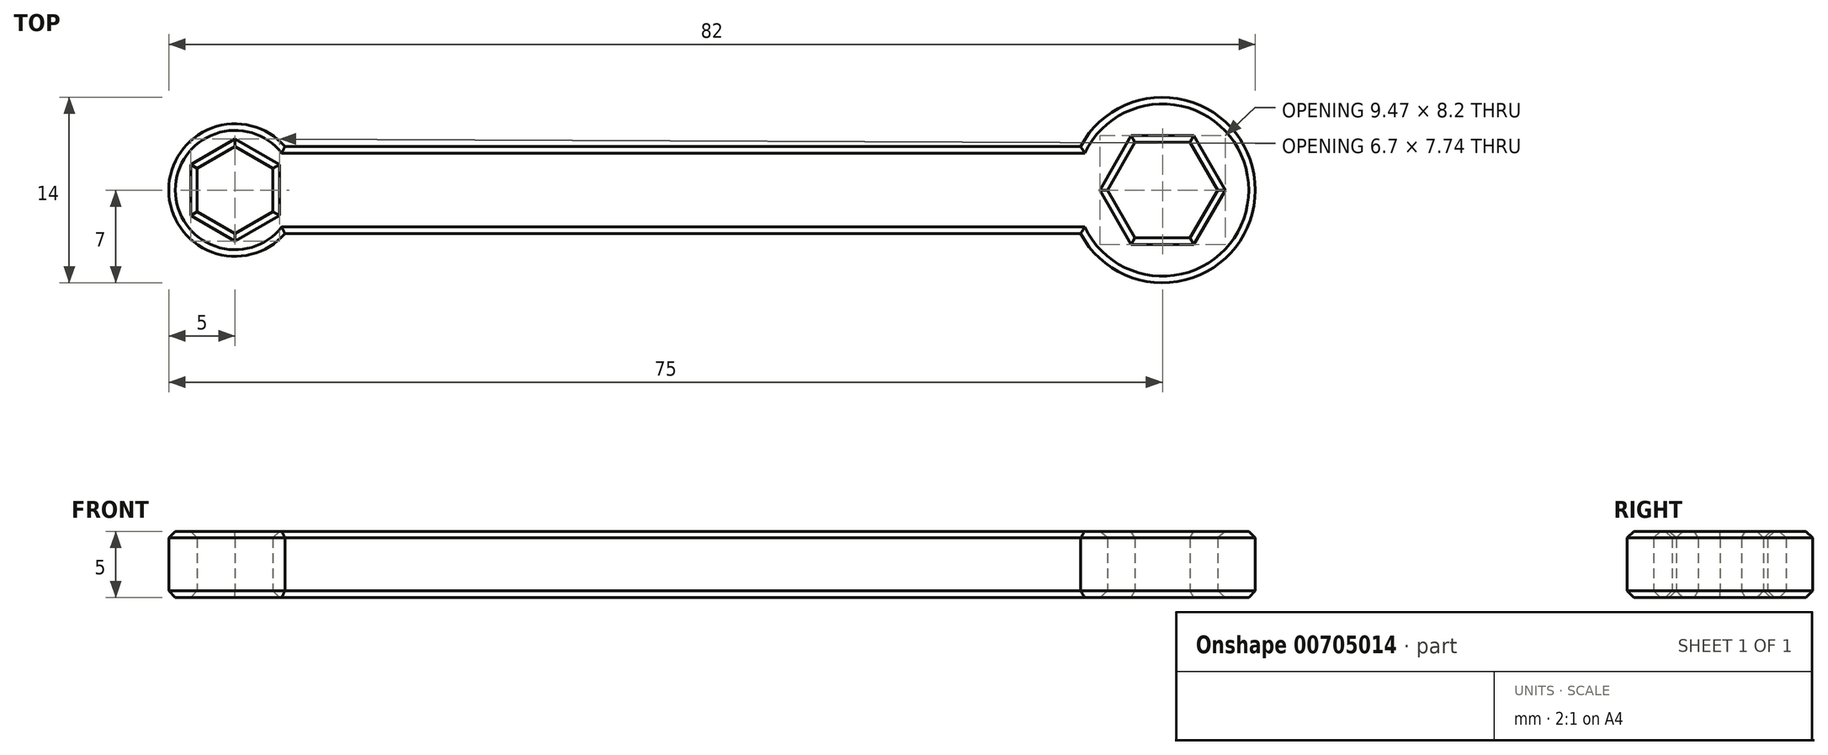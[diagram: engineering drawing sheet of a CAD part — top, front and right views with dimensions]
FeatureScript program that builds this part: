
annotation { "Feature Type Name" : "Feature", "Feature Type Description" : "" }
export const myFeature = defineFeature(function(context is Context, id is Id, definition is map)
    precondition{}
    {
        {
            var Q0;
            Q0=qCreatedBy(makeId("Top.planeOp"),FACE);
            var sketch = newSketch(context, id + "F0", { "sketchPlane" : qUnion([Q0])});
            skCircle(sketch, "E0.cCircle", {"center": v(-35, 0) * mm, "radius": 2.85 * mm, "construction": true});
            skLineSegment(sketch, "E0.0", {"start": v(-32.15, -1.65) * mm, "end": v(-35, -3.3) * mm});
            skLineSegment(sketch, "E0.1", {"start": v(-35, -3.3) * mm, "end": v(-37.85, -1.65) * mm});
            skLineSegment(sketch, "E0.2", {"start": v(-37.85, -1.65) * mm, "end": v(-37.85, 1.65) * mm});
            skLineSegment(sketch, "E0.3", {"start": v(-37.85, 1.65) * mm, "end": v(-35, 3.3) * mm});
            skLineSegment(sketch, "E0.4", {"start": v(-35, 3.3) * mm, "end": v(-32.15, 1.65) * mm});
            skLineSegment(sketch, "E0.5", {"start": v(-32.15, 1.65) * mm, "end": v(-32.15, -1.65) * mm});
            skPoint(sketch, "E0.0.midPoint", {"position": v(-33.58, -2.47) * mm});
            skCircle(sketch, "E1.cCircle", {"center": v(35, 0) * mm, "radius": 3.6 * mm, "construction": true});
            skLineSegment(sketch, "E1.0", {"start": v(37.08, -3.6) * mm, "end": v(32.92, -3.6) * mm});
            skLineSegment(sketch, "E1.1", {"start": v(32.92, -3.6) * mm, "end": v(30.84, 0) * mm});
            skLineSegment(sketch, "E1.2", {"start": v(30.84, 0) * mm, "end": v(32.92, 3.6) * mm});
            skLineSegment(sketch, "E1.3", {"start": v(32.92, 3.6) * mm, "end": v(37.08, 3.6) * mm});
            skLineSegment(sketch, "E1.4", {"start": v(37.08, 3.6) * mm, "end": v(39.16, 0) * mm});
            skLineSegment(sketch, "E1.5", {"start": v(39.16, 0) * mm, "end": v(37.08, -3.6) * mm});
            skPoint(sketch, "E1.0.midPoint", {"position": v(35, -3.6) * mm});
            skArc(sketch, "E2", {"start": v(-31.24, 3.3) * mm, "mid": v(-40, 0) * mm, "end": v(-31.24, -3.3) * mm});
            skArc(sketch, "E3", {"start": v(28.82, 3.3) * mm, "mid": v(42, 0) * mm, "end": v(28.82, -3.3) * mm});
            skLineSegment(sketch, "E4", {"start": v(-31.24, 3.3) * mm, "end": v(28.82, 3.3) * mm});
            skLineSegment(sketch, "E5", {"start": v(-31.24, -3.3) * mm, "end": v(28.82, -3.3) * mm});
            skSolve(sketch);
        }
        {
            var Q0;
            Q0 = qSketchRegion(id + "F0", true);
            extrude(context, id + "F1", {"entities" : qUnion([Q0]), "depth" : 5 * mm, "offsetDistance" : 25 * mm});
        }
        {
            var Q0;
            Q0=makeQuery(id+"F1.opExtrude","CAP_EDGE",EDGE,{"disambiguationData":[OSD([sQuery(id+"F0.wireOp",EDGE,"E0.3")])],"isStart":false});
            var Q1;
            Q1=makeQuery(id+"F1.opExtrude","CAP_EDGE",EDGE,{"disambiguationData":[OSD([sQuery(id+"F0.wireOp",EDGE,"E0.4")])],"isStart":false});
            var Q2;
            Q2=makeQuery(id+"F1.opExtrude","CAP_EDGE",EDGE,{"disambiguationData":[OSD([sQuery(id+"F0.wireOp",EDGE,"E0.5")])],"isStart":false});
            var Q3;
            Q3=makeQuery(id+"F1.opExtrude","CAP_EDGE",EDGE,{"disambiguationData":[OSD([sQuery(id+"F0.wireOp",EDGE,"E0.0")])],"isStart":false});
            var Q4;
            Q4=makeQuery(id+"F1.opExtrude","CAP_EDGE",EDGE,{"disambiguationData":[OSD([sQuery(id+"F0.wireOp",EDGE,"E0.1")])],"isStart":false});
            var Q5;
            Q5=makeQuery(id+"F1.opExtrude","CAP_EDGE",EDGE,{"disambiguationData":[OSD([sQuery(id+"F0.wireOp",EDGE,"E0.2")])],"isStart":false});
            var Q6;
            Q6=makeQuery(id+"F1.opExtrude","CAP_FACE",FACE,{"disambiguationData":[OSD([sQuery(id+"F0.wireOp",EDGE,"E0.0"),sQuery(id+"F0.wireOp",EDGE,"E0.1"),sQuery(id+"F0.wireOp",EDGE,"E0.2"),sQuery(id+"F0.wireOp",EDGE,"E0.3"),sQuery(id+"F0.wireOp",EDGE,"E0.4"),sQuery(id+"F0.wireOp",EDGE,"E0.5"),sQuery(id+"F0.wireOp",EDGE,"E1.0"),sQuery(id+"F0.wireOp",EDGE,"E1.1"),sQuery(id+"F0.wireOp",EDGE,"E1.2"),sQuery(id+"F0.wireOp",EDGE,"E1.3"),sQuery(id+"F0.wireOp",EDGE,"E1.4"),sQuery(id+"F0.wireOp",EDGE,"E1.5"),sQuery(id+"F0.wireOp",EDGE,"E2"),sQuery(id+"F0.wireOp",EDGE,"E3"),sQuery(id+"F0.wireOp",EDGE,"E4"),sQuery(id+"F0.wireOp",EDGE,"E5")])],"isStart":false});
            var Q7;
            Q7=makeQuery(id+"F1.opExtrude","CAP_FACE",FACE,{"disambiguationData":[OSD([sQuery(id+"F0.wireOp",EDGE,"E0.0"),sQuery(id+"F0.wireOp",EDGE,"E0.1"),sQuery(id+"F0.wireOp",EDGE,"E0.2"),sQuery(id+"F0.wireOp",EDGE,"E0.3"),sQuery(id+"F0.wireOp",EDGE,"E0.4"),sQuery(id+"F0.wireOp",EDGE,"E0.5"),sQuery(id+"F0.wireOp",EDGE,"E1.0"),sQuery(id+"F0.wireOp",EDGE,"E1.1"),sQuery(id+"F0.wireOp",EDGE,"E1.2"),sQuery(id+"F0.wireOp",EDGE,"E1.3"),sQuery(id+"F0.wireOp",EDGE,"E1.4"),sQuery(id+"F0.wireOp",EDGE,"E1.5"),sQuery(id+"F0.wireOp",EDGE,"E2"),sQuery(id+"F0.wireOp",EDGE,"E3"),sQuery(id+"F0.wireOp",EDGE,"E4"),sQuery(id+"F0.wireOp",EDGE,"E5")])],"isStart":true});
            chamfer(context, id + "F2", {"entities" : qUnion([Q0, Q1, Q2, Q3, Q4, Q5, Q6, Q7]), "width" : 0.5 * mm});
        }
    });
